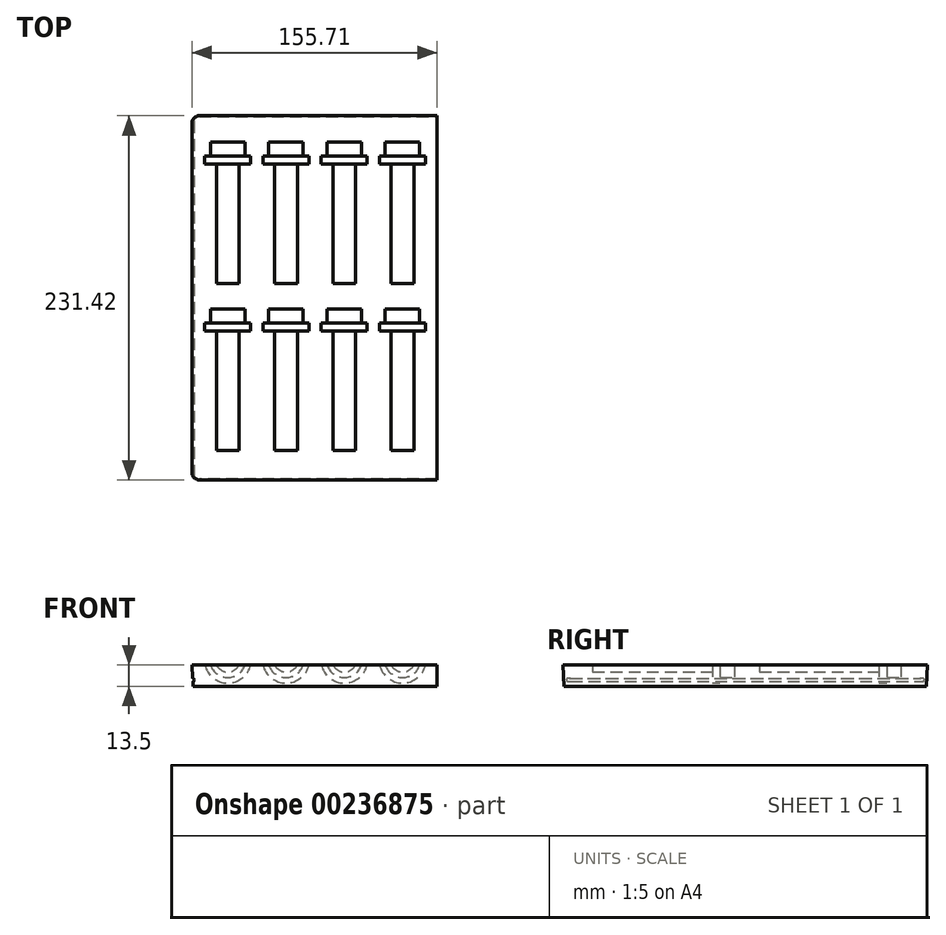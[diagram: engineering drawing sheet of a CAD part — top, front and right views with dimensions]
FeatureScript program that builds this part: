
annotation { "Feature Type Name" : "Feature", "Feature Type Description" : "" }
export const myFeature = defineFeature(function(context is Context, id is Id, definition is map)
    precondition{}
    {
        {
            var Q0;
            Q0=qCreatedBy(makeId("Top.planeOp"),FACE);
            var sketch = newSketch(context, id + "F0", { "sketchPlane" : qUnion([Q0])});
            skLineSegment(sketch, "E0.bottom", {"start": v(4, 0) * mm, "end": v(155, 0) * mm});
            skLineSegment(sketch, "E0.top", {"start": v(4, 230) * mm, "end": v(155, 230) * mm});
            skLineSegment(sketch, "E0.left", {"start": v(0, 4) * mm, "end": v(0, 226) * mm});
            skLineSegment(sketch, "E0.right", {"start": v(155, 0) * mm, "end": v(155, 230) * mm});
            skPoint(sketch, "E1.visualSharp", {"position": v(0, 230) * mm});
            skArc(sketch, "E1.filletArc", {"start": v(4, 230) * mm, "mid": v(1.17, 228.83) * mm, "end": v(0, 226) * mm});
            skPoint(sketch, "E2.visualSharp", {"position": v(0, 0) * mm});
            skArc(sketch, "E2.filletArc", {"start": v(0, 4) * mm, "mid": v(1.17, 1.17) * mm, "end": v(4, 0) * mm});
            skSolve(sketch);
        }
        {
            var Q0;
            Q0=makeQuery(id+"F0.imprint","IMPRINT",FACE,{"disambiguationData":[TD([[makeQuery(id+"F0.imprint","IMPRINT",EDGE,{"derivedFrom":sQuery(id+"F0.wireOp",EDGE,"E0.bottom")}),1.0]])]});
            extrude(context, id + "F1", {"entities" : qUnion([Q0]), "depth" : 17 * mm, "hasDraft" : true, "draftAngle" : 3 * degree});
        }
        {
            var Q0;
            Q0=qCreatedBy(makeId("Right.planeOp"),FACE);
            cPlane(context, id + "F2", {"entities" : qUnion([Q0]), "cplaneType" : CPlaneType.OFFSET, "offset" : 155 * mm, "width" : 150 * mm, "height" : 150 * mm});
        }
        {
            var Q0;
            Q0=qCreatedBy(id+"F2.planeOp",FACE);
            var sketch = newSketch(context, id + "F3", { "sketchPlane" : qUnion([Q0])});
            skLineSegment(sketch, "E3.0.0", {"start": v(0, 0) * mm, "end": v(230, 0) * mm});
            skLineSegment(sketch, "E3.0.1", {"start": v(230.9, 17) * mm, "end": v(230, 0) * mm});
            skLineSegment(sketch, "E3.0.2", {"start": v(-0.9, 17) * mm, "end": v(230.9, 17) * mm});
            skLineSegment(sketch, "E3.0.3", {"start": v(-0.9, 17) * mm, "end": v(0, 0) * mm});
            skSolve(sketch);
        }
        {
            var Q0;
            Q0 = qSketchRegion(id + "F3", true);
            extrude(context, id + "F4", {"entities" : qUnion([Q0]), "operationType" : NewBodyOperationType.REMOVE, "depth" : 25 * mm});
        }
        {
            var Q0;
            Q0=makeQuery(id+"F1.opExtrude","CAP_FACE",FACE,{"disambiguationData":[OSD([sQuery(id+"F0.wireOp",EDGE,"E0.bottom"),sQuery(id+"F0.wireOp",EDGE,"E0.top"),sQuery(id+"F0.wireOp",EDGE,"E0.left"),sQuery(id+"F0.wireOp",EDGE,"E0.right"),sQuery(id+"F0.wireOp",EDGE,"E1.filletArc"),sQuery(id+"F0.wireOp",EDGE,"E2.filletArc")])],"isStart":false});
            var sketch = newSketch(context, id + "F5", { "sketchPlane" : qUnion([Q0])});
            skLineSegment(sketch, "E4.bottom", {"start": v(0, 0) * mm, "end": v(22, 0) * mm, "construction": true});
            skLineSegment(sketch, "E4.top", {"start": v(0, 18) * mm, "end": v(22, 18) * mm, "construction": true});
            skLineSegment(sketch, "E4.left", {"start": v(0, 0) * mm, "end": v(0, 18) * mm, "construction": true});
            skLineSegment(sketch, "E4.right", {"start": v(22, 0) * mm, "end": v(22, 18) * mm, "construction": true});
            skLineSegment(sketch, "E5", {"start": v(22, 18) * mm, "end": v(59, 18) * mm, "construction": true});
            skLineSegment(sketch, "E6", {"start": v(59, 18) * mm, "end": v(96, 18) * mm, "construction": true});
            skLineSegment(sketch, "E7", {"start": v(96, 18) * mm, "end": v(133, 18) * mm, "construction": true});
            skLineSegment(sketch, "E8", {"start": v(133, 124) * mm, "end": v(96, 124) * mm, "construction": true});
            skLineSegment(sketch, "E9", {"start": v(96, 124) * mm, "end": v(59, 124) * mm, "construction": true});
            skLineSegment(sketch, "E10", {"start": v(59, 124) * mm, "end": v(22, 124) * mm, "construction": true});
            skPoint(sketch, "E10.endSnap0", {"position": v(77.5, 124) * mm});
            skLineSegment(sketch, "E11.bottom", {"start": v(22, 18) * mm, "end": v(30, 18) * mm});
            skLineSegment(sketch, "E11.left", {"start": v(22, 18) * mm, "end": v(22, 94) * mm});
            skLineSegment(sketch, "E11.right", {"start": v(30, 18) * mm, "end": v(30, 94) * mm});
            skLineSegment(sketch, "E12.bottom", {"start": v(30, 94) * mm, "end": v(37, 94) * mm});
            skLineSegment(sketch, "E12.top", {"start": v(33.5, 99) * mm, "end": v(37, 99) * mm});
            skLineSegment(sketch, "E12.left", {"start": v(22, 94) * mm, "end": v(22, 99) * mm});
            skLineSegment(sketch, "E12.right", {"start": v(37, 94) * mm, "end": v(37, 99) * mm});
            skLineSegment(sketch, "E13.top", {"start": v(22, 108) * mm, "end": v(33.5, 108) * mm});
            skLineSegment(sketch, "E13.left", {"start": v(22, 99) * mm, "end": v(22, 108) * mm});
            skLineSegment(sketch, "E13.right", {"start": v(33.5, 99) * mm, "end": v(33.5, 108) * mm});
            skLineSegment(sketch, "E14.bottom", {"start": v(59, 18) * mm, "end": v(67, 18) * mm});
            skLineSegment(sketch, "E14.left", {"start": v(59, 18) * mm, "end": v(59, 94) * mm});
            skLineSegment(sketch, "E14.right", {"start": v(67, 18) * mm, "end": v(67, 94) * mm});
            skLineSegment(sketch, "E15.bottom", {"start": v(67, 94) * mm, "end": v(74, 94) * mm});
            skLineSegment(sketch, "E15.top", {"start": v(70.5, 99) * mm, "end": v(74, 99) * mm});
            skLineSegment(sketch, "E15.left", {"start": v(59, 94) * mm, "end": v(59, 99) * mm});
            skLineSegment(sketch, "E15.right", {"start": v(74, 94) * mm, "end": v(74, 99) * mm});
            skLineSegment(sketch, "E16.top", {"start": v(59, 108) * mm, "end": v(70.5, 108) * mm});
            skLineSegment(sketch, "E16.left", {"start": v(59, 99) * mm, "end": v(59, 108) * mm});
            skLineSegment(sketch, "E16.right", {"start": v(70.5, 99) * mm, "end": v(70.5, 108) * mm});
            skLineSegment(sketch, "E17.bottom", {"start": v(96, 18) * mm, "end": v(104, 18) * mm});
            skLineSegment(sketch, "E17.left", {"start": v(96, 18) * mm, "end": v(96, 94) * mm});
            skLineSegment(sketch, "E17.right", {"start": v(104, 18) * mm, "end": v(104, 94) * mm});
            skLineSegment(sketch, "E18.bottom", {"start": v(104, 94) * mm, "end": v(111, 94) * mm});
            skLineSegment(sketch, "E18.top", {"start": v(107.5, 99) * mm, "end": v(111, 99) * mm});
            skLineSegment(sketch, "E18.left", {"start": v(96, 94) * mm, "end": v(96, 99) * mm});
            skLineSegment(sketch, "E18.right", {"start": v(111, 94) * mm, "end": v(111, 99) * mm});
            skLineSegment(sketch, "E19.top", {"start": v(96, 108) * mm, "end": v(107.5, 108) * mm});
            skLineSegment(sketch, "E19.left", {"start": v(96, 99) * mm, "end": v(96, 108) * mm});
            skLineSegment(sketch, "E19.right", {"start": v(107.5, 99) * mm, "end": v(107.5, 108) * mm});
            skLineSegment(sketch, "E20.bottom", {"start": v(133, 18) * mm, "end": v(141, 18) * mm});
            skLineSegment(sketch, "E20.left", {"start": v(133, 18) * mm, "end": v(133, 94) * mm});
            skLineSegment(sketch, "E20.right", {"start": v(141, 18) * mm, "end": v(141, 94) * mm});
            skLineSegment(sketch, "E21.bottom", {"start": v(141, 94) * mm, "end": v(148, 94) * mm});
            skLineSegment(sketch, "E21.top", {"start": v(144.5, 99) * mm, "end": v(148, 99) * mm});
            skLineSegment(sketch, "E21.left", {"start": v(133, 94) * mm, "end": v(133, 99) * mm});
            skLineSegment(sketch, "E21.right", {"start": v(148, 94) * mm, "end": v(148, 99) * mm});
            skLineSegment(sketch, "E22.top", {"start": v(133, 108) * mm, "end": v(144.5, 108) * mm});
            skLineSegment(sketch, "E22.left", {"start": v(133, 99) * mm, "end": v(133, 108) * mm});
            skLineSegment(sketch, "E22.right", {"start": v(144.5, 99) * mm, "end": v(144.5, 108) * mm});
            skLineSegment(sketch, "E23.bottom", {"start": v(22, 124) * mm, "end": v(30, 124) * mm});
            skLineSegment(sketch, "E23.left", {"start": v(22, 124) * mm, "end": v(22, 200) * mm});
            skLineSegment(sketch, "E23.right", {"start": v(30, 124) * mm, "end": v(30, 200) * mm});
            skLineSegment(sketch, "E24.bottom", {"start": v(30, 200) * mm, "end": v(37, 200) * mm});
            skLineSegment(sketch, "E24.top", {"start": v(33.5, 205) * mm, "end": v(37, 205) * mm});
            skLineSegment(sketch, "E24.left", {"start": v(22, 200) * mm, "end": v(22, 205) * mm});
            skLineSegment(sketch, "E24.right", {"start": v(37, 200) * mm, "end": v(37, 205) * mm});
            skLineSegment(sketch, "E25.top", {"start": v(22, 214) * mm, "end": v(33.5, 214) * mm});
            skLineSegment(sketch, "E25.left", {"start": v(22, 205) * mm, "end": v(22, 214) * mm});
            skLineSegment(sketch, "E25.right", {"start": v(33.5, 205) * mm, "end": v(33.5, 214) * mm});
            skLineSegment(sketch, "E26.bottom", {"start": v(59, 124) * mm, "end": v(67, 124) * mm});
            skLineSegment(sketch, "E26.left", {"start": v(59, 124) * mm, "end": v(59, 200) * mm});
            skLineSegment(sketch, "E26.right", {"start": v(67, 124) * mm, "end": v(67, 200) * mm});
            skLineSegment(sketch, "E27.bottom", {"start": v(67, 200) * mm, "end": v(74, 200) * mm});
            skLineSegment(sketch, "E27.top", {"start": v(70.5, 205) * mm, "end": v(74, 205) * mm});
            skLineSegment(sketch, "E27.left", {"start": v(59, 200) * mm, "end": v(59, 205) * mm});
            skLineSegment(sketch, "E27.right", {"start": v(74, 200) * mm, "end": v(74, 205) * mm});
            skLineSegment(sketch, "E28.top", {"start": v(59, 214) * mm, "end": v(70.5, 214) * mm});
            skLineSegment(sketch, "E28.left", {"start": v(59, 205) * mm, "end": v(59, 214) * mm});
            skLineSegment(sketch, "E28.right", {"start": v(70.5, 205) * mm, "end": v(70.5, 214) * mm});
            skLineSegment(sketch, "E29.bottom", {"start": v(96, 124) * mm, "end": v(104, 124) * mm});
            skLineSegment(sketch, "E29.left", {"start": v(96, 124) * mm, "end": v(96, 200) * mm});
            skLineSegment(sketch, "E29.right", {"start": v(104, 124) * mm, "end": v(104, 200) * mm});
            skLineSegment(sketch, "E30.bottom", {"start": v(104, 200) * mm, "end": v(111, 200) * mm});
            skLineSegment(sketch, "E30.top", {"start": v(107.5, 205) * mm, "end": v(111, 205) * mm});
            skLineSegment(sketch, "E30.left", {"start": v(96, 200) * mm, "end": v(96, 205) * mm});
            skLineSegment(sketch, "E30.right", {"start": v(111, 200) * mm, "end": v(111, 205) * mm});
            skLineSegment(sketch, "E31.top", {"start": v(96, 214) * mm, "end": v(107.5, 214) * mm});
            skLineSegment(sketch, "E31.left", {"start": v(96, 205) * mm, "end": v(96, 214) * mm});
            skLineSegment(sketch, "E31.right", {"start": v(107.5, 205) * mm, "end": v(107.5, 214) * mm});
            skLineSegment(sketch, "E32.bottom", {"start": v(133, 124) * mm, "end": v(141, 124) * mm});
            skLineSegment(sketch, "E32.left", {"start": v(133, 124) * mm, "end": v(133, 200) * mm});
            skLineSegment(sketch, "E32.right", {"start": v(141, 124) * mm, "end": v(141, 200) * mm});
            skLineSegment(sketch, "E33.bottom", {"start": v(141, 200) * mm, "end": v(148, 200) * mm});
            skLineSegment(sketch, "E33.top", {"start": v(144.5, 205) * mm, "end": v(148, 205) * mm});
            skLineSegment(sketch, "E33.left", {"start": v(133, 200) * mm, "end": v(133, 205) * mm});
            skLineSegment(sketch, "E33.right", {"start": v(148, 200) * mm, "end": v(148, 205) * mm});
            skLineSegment(sketch, "E34.top", {"start": v(133, 214) * mm, "end": v(144.5, 214) * mm});
            skLineSegment(sketch, "E34.left", {"start": v(133, 205) * mm, "end": v(133, 214) * mm});
            skLineSegment(sketch, "E34.right", {"start": v(144.5, 205) * mm, "end": v(144.5, 214) * mm});
            skSolve(sketch);
        }
        {
            var Q0;
            Q0=makeQuery(id+"F5.imprint","IMPRINT",FACE,{"disambiguationData":[TD([[makeQuery(id+"F5.imprint","IMPRINT",EDGE,{"derivedFrom":sQuery(id+"F5.wireOp",EDGE,"E11.bottom")}),1.0]])]});
            var Q1;
            Q1=sQuery(id+"F5.wireOp",EDGE,"E11.left");
            revolve(context, id + "F6", {"operationType" : NewBodyOperationType.REMOVE, "entities" : qUnion([Q0]), "axis" : qUnion([Q1]), "revolveType" : RevolveType.FULL, "oppositeDirection" : true});
        }
        {
            var Q0;
            Q0=makeQuery(id+"F5.imprint","IMPRINT",FACE,{"disambiguationData":[TD([[makeQuery(id+"F5.imprint","IMPRINT",EDGE,{"derivedFrom":sQuery(id+"F5.wireOp",EDGE,"E14.bottom")}),1.0]])]});
            var Q1;
            Q1=sQuery(id+"F5.wireOp",EDGE,"E14.left");
            revolve(context, id + "F7", {"operationType" : NewBodyOperationType.REMOVE, "entities" : qUnion([Q0]), "axis" : qUnion([Q1]), "revolveType" : RevolveType.FULL, "oppositeDirection" : true});
        }
        {
            var Q0;
            Q0=makeQuery(id+"F5.imprint","IMPRINT",FACE,{"disambiguationData":[TD([[makeQuery(id+"F5.imprint","IMPRINT",EDGE,{"derivedFrom":sQuery(id+"F5.wireOp",EDGE,"E17.bottom")}),1.0]])]});
            var Q1;
            Q1=sQuery(id+"F5.wireOp",EDGE,"E17.left");
            revolve(context, id + "F8", {"operationType" : NewBodyOperationType.REMOVE, "entities" : qUnion([Q0]), "axis" : qUnion([Q1]), "revolveType" : RevolveType.FULL, "oppositeDirection" : true});
        }
        {
            var Q0;
            Q0=makeQuery(id+"F5.imprint","IMPRINT",FACE,{"disambiguationData":[TD([[makeQuery(id+"F5.imprint","IMPRINT",EDGE,{"derivedFrom":sQuery(id+"F5.wireOp",EDGE,"E20.bottom")}),1.0]])]});
            var Q1;
            Q1=sQuery(id+"F5.wireOp",EDGE,"E20.left");
            revolve(context, id + "F9", {"operationType" : NewBodyOperationType.REMOVE, "entities" : qUnion([Q0]), "axis" : qUnion([Q1]), "revolveType" : RevolveType.FULL, "oppositeDirection" : true});
        }
        {
            var Q0;
            Q0=makeQuery(id+"F5.imprint","IMPRINT",FACE,{"disambiguationData":[TD([[makeQuery(id+"F5.imprint","IMPRINT",EDGE,{"derivedFrom":sQuery(id+"F5.wireOp",EDGE,"E23.bottom")}),1.0]])]});
            var Q1;
            Q1=sQuery(id+"F5.wireOp",EDGE,"E23.left");
            revolve(context, id + "F10", {"operationType" : NewBodyOperationType.REMOVE, "entities" : qUnion([Q0]), "axis" : qUnion([Q1]), "revolveType" : RevolveType.FULL, "oppositeDirection" : true});
        }
        {
            var Q0;
            Q0=makeQuery(id+"F5.imprint","IMPRINT",FACE,{"disambiguationData":[TD([[makeQuery(id+"F5.imprint","IMPRINT",EDGE,{"derivedFrom":sQuery(id+"F5.wireOp",EDGE,"E26.bottom")}),1.0]])]});
            var Q1;
            Q1=sQuery(id+"F5.wireOp",EDGE,"E26.left");
            revolve(context, id + "F11", {"operationType" : NewBodyOperationType.REMOVE, "entities" : qUnion([Q0]), "axis" : qUnion([Q1]), "revolveType" : RevolveType.FULL, "oppositeDirection" : true});
        }
        {
            var Q0;
            Q0=makeQuery(id+"F5.imprint","IMPRINT",FACE,{"disambiguationData":[TD([[makeQuery(id+"F5.imprint","IMPRINT",EDGE,{"derivedFrom":sQuery(id+"F5.wireOp",EDGE,"E29.bottom")}),1.0]])]});
            var Q1;
            Q1=sQuery(id+"F5.wireOp",EDGE,"E29.left");
            revolve(context, id + "F12", {"operationType" : NewBodyOperationType.REMOVE, "entities" : qUnion([Q0]), "axis" : qUnion([Q1]), "revolveType" : RevolveType.FULL, "oppositeDirection" : true});
        }
        {
            var Q0;
            Q0=makeQuery(id+"F5.imprint","IMPRINT",FACE,{"disambiguationData":[TD([[makeQuery(id+"F5.imprint","IMPRINT",EDGE,{"derivedFrom":sQuery(id+"F5.wireOp",EDGE,"E32.bottom")}),1.0]])]});
            var Q1;
            Q1=sQuery(id+"F5.wireOp",EDGE,"E32.left");
            revolve(context, id + "F13", {"operationType" : NewBodyOperationType.REMOVE, "entities" : qUnion([Q0]), "axis" : qUnion([Q1]), "revolveType" : RevolveType.FULL, "oppositeDirection" : true});
        }
        {
            var Q0;
            Q0=makeQuery(id+"F1.opExtrude","SWEPT_FACE",FACE,{"disambiguationData":[OSD([sQuery(id+"F0.wireOp",EDGE,"E0.left")])]});
            var sketch = newSketch(context, id + "F14", { "sketchPlane" : qUnion([Q0])});
            skLineSegment(sketch, "E35", {"start": v(-226, 0) * mm, "end": v(-226, 4) * mm, "construction": true});
            skLineSegment(sketch, "E36", {"start": v(-226, 4) * mm, "end": v(-4, 4) * mm, "construction": true});
            skLineSegment(sketch, "E37", {"start": v(-226, 4) * mm, "end": v(-231, 4) * mm});
            skLineSegment(sketch, "E38", {"start": v(-231, 4) * mm, "end": v(-231, 3) * mm});
            skLineSegment(sketch, "E39", {"start": v(-231, 3) * mm, "end": v(2, 3) * mm});
            skLineSegment(sketch, "E40", {"start": v(2, 3) * mm, "end": v(2, 4) * mm});
            skLineSegment(sketch, "E41", {"start": v(2, 4) * mm, "end": v(-226, 4) * mm});
            skSolve(sketch);
        }
        {
            var Q0;
            Q0 = qSketchRegion(id + "F14", true);
            var Q1;
            Q1=sQuery(id+"F14.wireOp",EDGE,"E41");
            revolve(context, id + "F15", {"operationType" : NewBodyOperationType.REMOVE, "entities" : qUnion([Q0]), "axis" : qUnion([Q1]), "revolveType" : RevolveType.FULL, "oppositeDirection" : true});
        }
        {
            var Q0;
            Q0=makeQuery(id+"F3.imprint","IMPRINT",FACE,{"disambiguationData":[TD([[makeQuery(id+"F3.imprint","IMPRINT",EDGE,{"derivedFrom":sQuery(id+"F3.wireOp",EDGE,"E3.0.0")}),1.0]])]});
            var sketch = newSketch(context, id + "F16", { "sketchPlane" : qUnion([Q0])});
            skLineSegment(sketch, "E42", {"start": v(0, 0) * mm, "end": v(-10, 0) * mm, "construction": true});
            skLineSegment(sketch, "E43", {"start": v(-10, 0) * mm, "end": v(-10, 13.5) * mm, "construction": true});
            skLineSegment(sketch, "E44.bottom", {"start": v(-10, 13.5) * mm, "end": v(236.07, 13.5) * mm});
            skLineSegment(sketch, "E44.top", {"start": v(-10, 22.67) * mm, "end": v(236.07, 22.67) * mm});
            skLineSegment(sketch, "E44.left", {"start": v(-10, 13.5) * mm, "end": v(-10, 22.67) * mm});
            skLineSegment(sketch, "E44.right", {"start": v(236.07, 13.5) * mm, "end": v(236.07, 22.67) * mm});
            skSolve(sketch);
        }
        {
            var Q0;
            Q0 = qSketchRegion(id + "F16", true);
            extrude(context, id + "F17", {"entities" : qUnion([Q0]), "operationType" : NewBodyOperationType.REMOVE, "endBound" : BoundingType.THROUGH_ALL, "oppositeDirection" : true, "depth" : 25 * mm});
        }
    });
